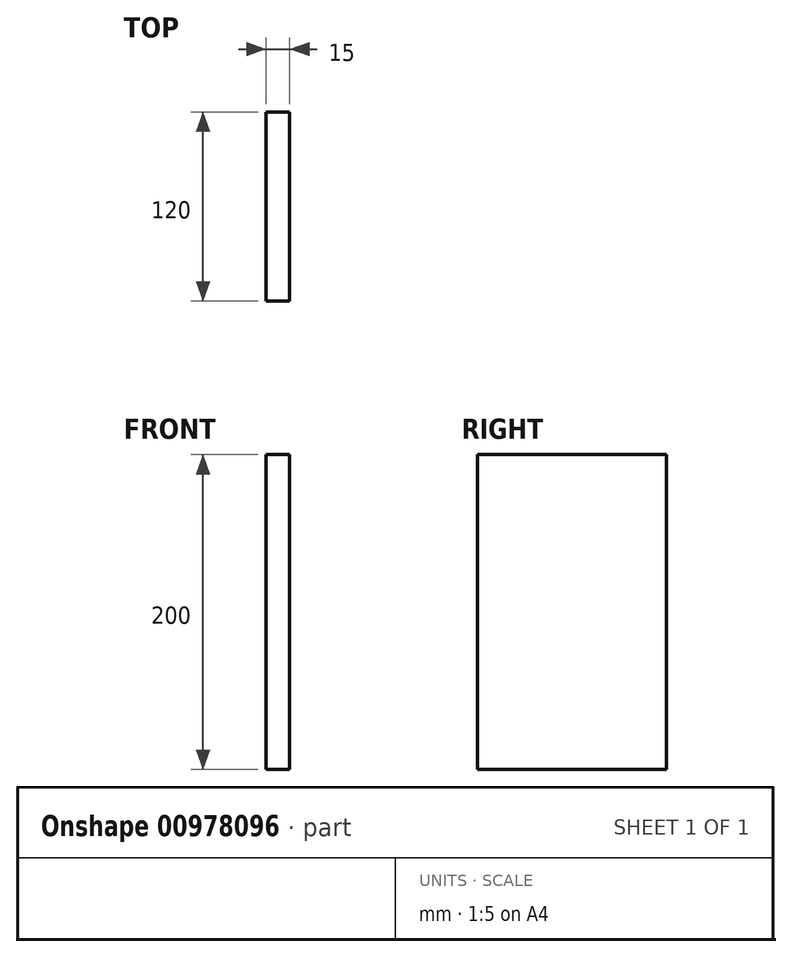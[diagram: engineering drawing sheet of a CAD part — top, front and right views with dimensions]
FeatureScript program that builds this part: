
annotation { "Feature Type Name" : "Feature", "Feature Type Description" : "" }
export const myFeature = defineFeature(function(context is Context, id is Id, definition is map)
    precondition{}
    {
        {
            var Q0;
            Q0=qCreatedBy(makeId("Right.planeOp"),FACE);
            var sketch = newSketch(context, id + "F0", { "sketchPlane" : qUnion([Q0])});
            skLineSegment(sketch, "E0.bottom", {"start": v(-60, 100) * mm, "end": v(60, 100) * mm});
            skLineSegment(sketch, "E0.top", {"start": v(-60, -100) * mm, "end": v(60, -100) * mm});
            skLineSegment(sketch, "E0.left", {"start": v(-60, 100) * mm, "end": v(-60, -100) * mm});
            skLineSegment(sketch, "E0.right", {"start": v(60, 100) * mm, "end": v(60, -100) * mm});
            skPoint(sketch, "E0.middle", {"position": v(0, 0) * mm});
            skSolve(sketch);
        }
        {
            var Q0;
            Q0 = qSketchRegion(id + "F0", true);
            extrude(context, id + "F1", {"entities" : qUnion([Q0]), "endBound" : BoundingType.SYMMETRIC, "depth" : 15 * mm, "offsetDistance" : 25 * mm});
        }
    });
